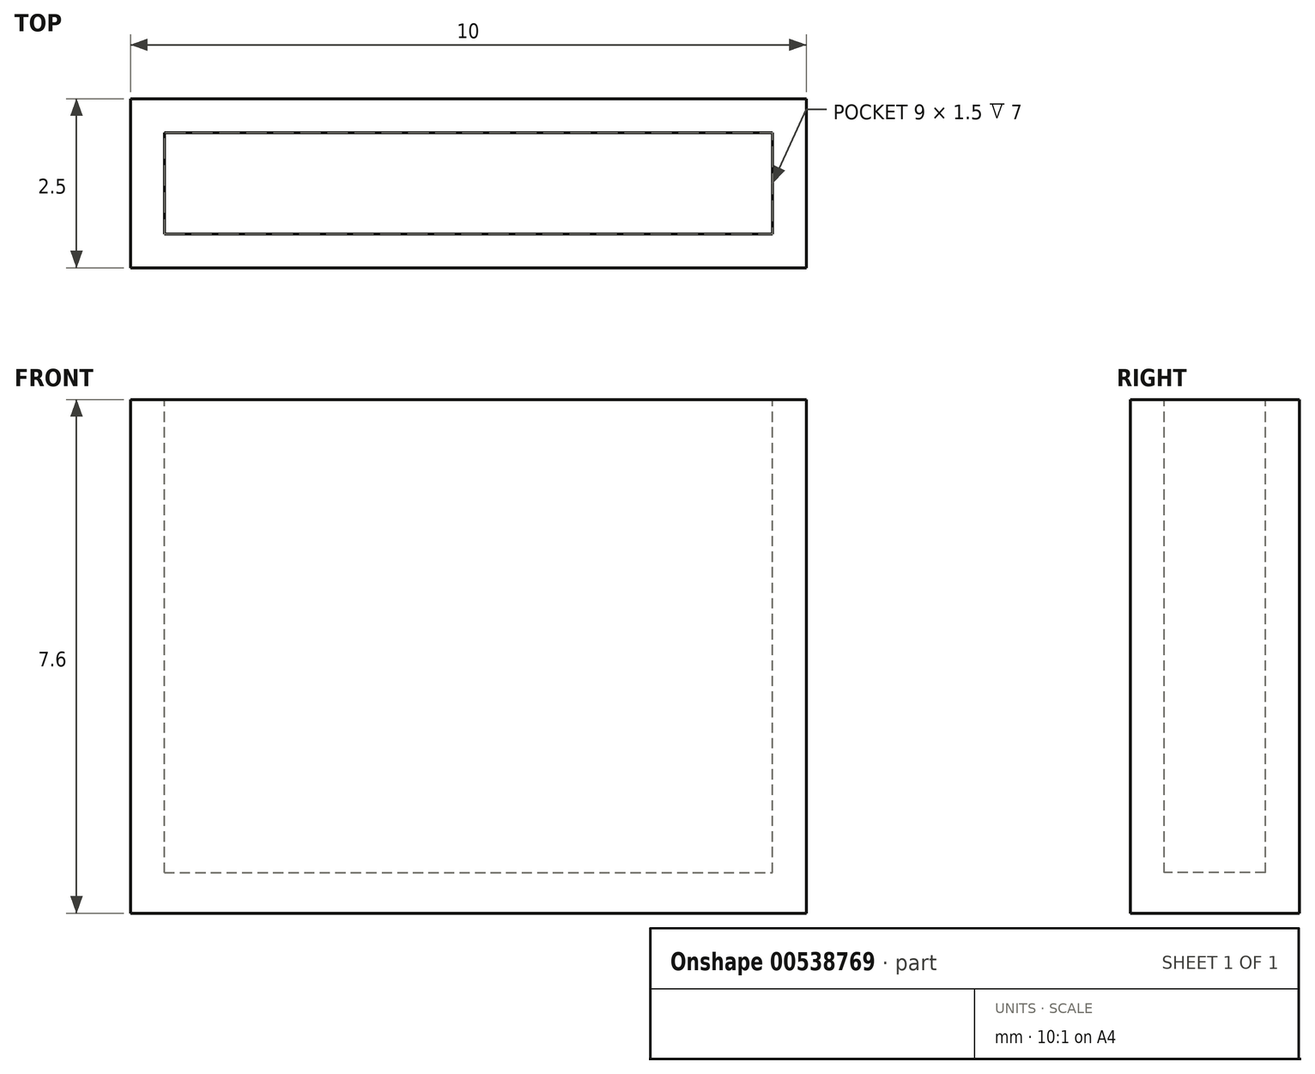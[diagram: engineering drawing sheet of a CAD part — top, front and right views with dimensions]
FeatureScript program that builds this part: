
annotation { "Feature Type Name" : "Feature", "Feature Type Description" : "" }
export const myFeature = defineFeature(function(context is Context, id is Id, definition is map)
    precondition{}
    {
        {
            var Q0;
            Q0=qCreatedBy(makeId("Top.planeOp"),FACE);
            var sketch = newSketch(context, id + "F0", { "sketchPlane" : qUnion([Q0])});
            skLineSegment(sketch, "E0", {"start": v(0, 0) * mm, "end": v(10, 0) * mm});
            skLineSegment(sketch, "E1", {"start": v(10, 0) * mm, "end": v(10, 2.5) * mm});
            skLineSegment(sketch, "E2", {"start": v(10, 2.5) * mm, "end": v(0, 2.5) * mm});
            skLineSegment(sketch, "E3", {"start": v(0, 2.5) * mm, "end": v(0, 0) * mm});
            skSolve(sketch);
        }
        {
            var Q0;
            Q0 = qSketchRegion(id + "F0", true);
            extrude(context, id + "F1", {"entities" : qUnion([Q0]), "depth" : 7.6 * mm, "offsetDistance" : 25 * mm});
        }
        {
            var Q0;
            Q0=makeQuery(id+"F1.opExtrude","CAP_FACE",FACE,{"disambiguationData":[OSD([sQuery(id+"F0.wireOp",EDGE,"E0"),sQuery(id+"F0.wireOp",EDGE,"E1"),sQuery(id+"F0.wireOp",EDGE,"E2"),sQuery(id+"F0.wireOp",EDGE,"E3")])],"isStart":false});
            var sketch = newSketch(context, id + "F2", { "sketchPlane" : qUnion([Q0])});
            skLineSegment(sketch, "E4.bottom", {"start": v(0.5, 2) * mm, "end": v(9.5, 2) * mm});
            skLineSegment(sketch, "E4.top", {"start": v(0.5, 0.5) * mm, "end": v(9.5, 0.5) * mm});
            skLineSegment(sketch, "E4.left", {"start": v(0.5, 2) * mm, "end": v(0.5, 0.5) * mm});
            skLineSegment(sketch, "E4.right", {"start": v(9.5, 2) * mm, "end": v(9.5, 0.5) * mm});
            skSolve(sketch);
        }
        {
            var Q0;
            Q0 = qSketchRegion(id + "F2", true);
            extrude(context, id + "F3", {"entities" : qUnion([Q0]), "operationType" : NewBodyOperationType.REMOVE, "oppositeDirection" : true, "depth" : 7 * mm, "offsetDistance" : 25 * mm});
        }
    });
